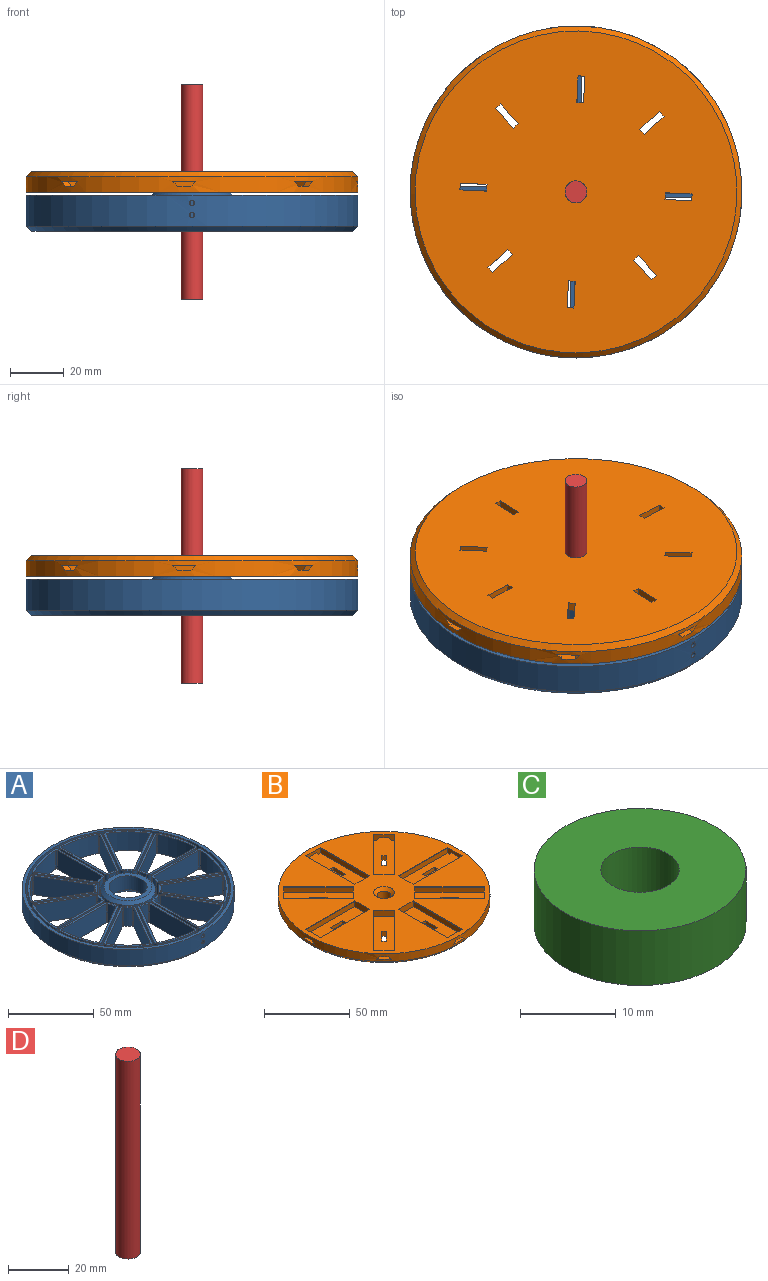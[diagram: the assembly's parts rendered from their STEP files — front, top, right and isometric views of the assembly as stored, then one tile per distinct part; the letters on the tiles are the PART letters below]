
ASSEMBLY  parts=4 mates=4
PART A: 223 faces, bbox 123.9x123.9x14.7 mm
  f0: plane 119.88x119.88mm, normal (0,0,1), area 1334.9mm2, adj f4,f6,f7,f8,f9,f10,f11,f12
  f1: cylinder r=11.1mm len=22.2mm, axis (0,0,-1), area 700mm2, adj f211,f213
  f2: cylinder r=61.94mm len=123.88mm, axis (0,0,-1), area 4468.3mm2, adj f5,f212,f215,f216,f217,f218,f219,f220
  f3: plane 120.15x120.15mm, normal (0,0,-1), area 3116.5mm2, adj f114,f115,f116,f117,f118,f119,f120,f121
  f4: cylinder r=59.94mm len=119.88mm, axis (0,0,-1), area 3758.9mm2, adj f0,f5,f215,f216,f217,f218,f219,f220
  f5: plane 123.88x123.88mm, normal (0,0,1), area 765.8mm2, adj f2,f4
  f6: plane 36.7x10mm, normal (0,1,0), area 367mm2, adj f0,f7,f13,f14
  f7: cylinder r=2mm len=10mm, axis (0,0,-1), area 28.8mm2, adj f0,f6,f8,f14
  f8: cylinder r=18.01mm len=10mm, axis (0,0,-1), area 47.4mm2, adj f0,f7,f9,f14
  f9: cylinder r=2mm len=10mm, axis (0,0,-1), area 28.8mm2, adj f0,f8,f10,f14
  f10: plane 31.79x18.35mm, normal (-0.5,-0.87,0), area 367mm2, adj f0,f9,f11,f14
  f11: cylinder r=2mm len=10mm, axis (0,0,-1), area 32.3mm2, adj f0,f10,f12,f14
  f12: cylinder r=58.6mm len=24.25mm, axis (0,0,-1), area 253mm2, adj f0,f11,f13,f14
  f13: cylinder r=2mm len=10mm, axis (0,0,-1), area 32.3mm2, adj f0,f6,f12,f14
  f14: plane 42.06x27.42mm, normal (0,0,1), area 145.1mm2, adj f6,f7,f8,f9,f10,f11,f12,f13
  f15: plane 31.79x18.35mm, normal (-0.5,0.87,0), area 367mm2, adj f0,f16,f22,f23
  f16: cylinder r=2mm len=10mm, axis (0,0,-1), area 28.8mm2, adj f0,f15,f17,f23
  f17: cylinder r=18.01mm len=10mm, axis (0,0,-1), area 47.4mm2, adj f0,f16,f18,f23
  f18: cylinder r=2mm len=10mm, axis (0,0,-1), area 28.8mm2, adj f0,f17,f19,f23
  f19: plane 36.7x10mm, normal (0,-1,0), area 367mm2, adj f0,f18,f20,f23
  f20: cylinder r=2mm len=10mm, axis (0,0,-1), area 32.3mm2, adj f0,f19,f21,f23
  f21: cylinder r=58.6mm len=24.25mm, axis (0,0,-1), area 253mm2, adj f0,f20,f22,f23
  f22: cylinder r=2mm len=10mm, axis (0,0,-1), area 32.3mm2, adj f0,f15,f21,f23
  f23: plane 42.06x27.42mm, normal (0,0,1), area 145.1mm2, adj f15,f16,f17,f18,f19,f20,f21,f22
  f24: plane 31.79x18.35mm, normal (-0.87,0.5,0), area 367mm2, adj f0,f25,f31,f32
  f25: cylinder r=2mm len=10mm, axis (0,0,-1), area 28.8mm2, adj f0,f24,f26,f32
  f26: cylinder r=18.01mm len=10mm, axis (0,0,-1), area 47.4mm2, adj f0,f25,f27,f32
  f27: cylinder r=2mm len=10mm, axis (0,0,-1), area 28.8mm2, adj f0,f26,f28,f32
  f28: plane 31.79x18.35mm, normal (0.5,-0.87,0), area 367mm2, adj f0,f27,f29,f32
  f29: cylinder r=2mm len=10mm, axis (0,0,-1), area 32.3mm2, adj f0,f28,f30,f32
  f30: cylinder r=58.6mm len=17.75mm, axis (0,0,-1), area 253mm2, adj f0,f29,f31,f32
  f31: cylinder r=2mm len=10mm, axis (0,0,-1), area 32.3mm2, adj f0,f24,f30,f32
  f32: plane 39.5x39.5mm, normal (0,0,1), area 145.1mm2, adj f24,f25,f26,f27,f28,f29,f30,f31
  f33: plane 36.7x10mm, normal (-1,0,0), area 367mm2, adj f0,f34,f40,f41
  f34: cylinder r=2mm len=10mm, axis (0,0,-1), area 28.8mm2, adj f0,f33,f35,f41
  f35: cylinder r=18.01mm len=10mm, axis (0,0,-1), area 47.4mm2, adj f0,f34,f36,f41
  f36: cylinder r=2mm len=10mm, axis (0,0,-1), area 28.8mm2, adj f0,f35,f37,f41
  f37: plane 31.79x18.35mm, normal (0.87,-0.5,0), area 367mm2, adj f0,f36,f38,f41
  f38: cylinder r=2mm len=10mm, axis (0,0,-1), area 32.3mm2, adj f0,f37,f39,f41
  f39: cylinder r=58.6mm len=24.25mm, axis (0,0,-1), area 253mm2, adj f0,f38,f40,f41
  f40: cylinder r=2mm len=10mm, axis (0,0,-1), area 32.3mm2, adj f0,f33,f39,f41
  f41: plane 42.06x27.42mm, normal (0,0,1), area 145.1mm2, adj f33,f34,f35,f36,f37,f38,f39,f40
  f42: plane 31.79x18.35mm, normal (-0.87,-0.5,0), area 367mm2, adj f0,f43,f49,f50
  f43: cylinder r=2mm len=10mm, axis (0,0,-1), area 28.8mm2, adj f0,f42,f44,f50
  f44: cylinder r=18.01mm len=10mm, axis (0,0,-1), area 47.4mm2, adj f0,f43,f45,f50
  f45: cylinder r=2mm len=10mm, axis (0,0,-1), area 28.8mm2, adj f0,f44,f46,f50
  f46: plane 36.7x10mm, normal (1,0,0), area 367mm2, adj f0,f45,f47,f50
  f47: cylinder r=2mm len=10mm, axis (0,0,-1), area 32.3mm2, adj f0,f46,f48,f50
  f48: cylinder r=58.6mm len=24.25mm, axis (0,0,-1), area 253mm2, adj f0,f47,f49,f50
  f49: cylinder r=2mm len=10mm, axis (0,0,-1), area 32.3mm2, adj f0,f42,f48,f50
  f50: plane 42.06x27.42mm, normal (0,0,1), area 145.1mm2, adj f42,f43,f44,f45,f46,f47,f48,f49
  f51: plane 31.79x18.35mm, normal (-0.5,-0.87,0), area 367mm2, adj f0,f52,f58,f59
  f52: cylinder r=2mm len=10mm, axis (0,0,-1), area 28.8mm2, adj f0,f51,f53,f59
  f53: cylinder r=18.01mm len=10mm, axis (0,0,-1), area 47.4mm2, adj f0,f52,f54,f59
  f54: cylinder r=2mm len=10mm, axis (0,0,-1), area 28.8mm2, adj f0,f53,f55,f59
  f55: plane 31.79x18.35mm, normal (0.87,0.5,0), area 367mm2, adj f0,f54,f56,f59
  f56: cylinder r=2mm len=10mm, axis (0,0,-1), area 32.3mm2, adj f0,f55,f57,f59
  f57: cylinder r=58.6mm len=17.75mm, axis (0,0,-1), area 253mm2, adj f0,f56,f58,f59
  f58: cylinder r=2mm len=10mm, axis (0,0,-1), area 32.3mm2, adj f0,f51,f57,f59
  f59: plane 39.5x39.5mm, normal (0,0,1), area 145.1mm2, adj f51,f52,f53,f54,f55,f56,f57,f58
  f60: plane 36.7x10mm, normal (0,-1,0), area 367mm2, adj f0,f61,f67,f68
  f61: cylinder r=2mm len=10mm, axis (0,0,-1), area 28.8mm2, adj f0,f60,f62,f68
  f62: cylinder r=18.01mm len=10mm, axis (0,0,-1), area 47.4mm2, adj f0,f61,f63,f68
  f63: cylinder r=2mm len=10mm, axis (0,0,-1), area 28.8mm2, adj f0,f62,f64,f68
  f64: plane 31.79x18.35mm, normal (0.5,0.87,0), area 367mm2, adj f0,f63,f65,f68
  f65: cylinder r=2mm len=10mm, axis (0,0,-1), area 32.3mm2, adj f0,f64,f66,f68
  f66: cylinder r=58.6mm len=24.25mm, axis (0,0,-1), area 253mm2, adj f0,f65,f67,f68
  f67: cylinder r=2mm len=10mm, axis (0,0,-1), area 32.3mm2, adj f0,f60,f66,f68
  f68: plane 42.06x27.42mm, normal (0,0,1), area 145.1mm2, adj f60,f61,f62,f63,f64,f65,f66,f67
  f69: plane 31.79x18.35mm, normal (0.5,-0.87,0), area 367mm2, adj f0,f70,f76,f77
  f70: cylinder r=2mm len=10mm, axis (0,0,-1), area 28.8mm2, adj f0,f69,f71,f77
  f71: cylinder r=18.01mm len=10mm, axis (0,0,-1), area 47.4mm2, adj f0,f70,f72,f77
  f72: cylinder r=2mm len=10mm, axis (0,0,-1), area 28.8mm2, adj f0,f71,f73,f77
  f73: plane 36.7x10mm, normal (0,1,0), area 367mm2, adj f0,f72,f74,f77
  f74: cylinder r=2mm len=10mm, axis (0,0,-1), area 32.3mm2, adj f0,f73,f75,f77
  f75: cylinder r=58.6mm len=24.25mm, axis (0,0,-1), area 253mm2, adj f0,f74,f76,f77
  f76: cylinder r=2mm len=10mm, axis (0,0,-1), area 32.3mm2, adj f0,f69,f75,f77
  f77: plane 42.06x27.42mm, normal (0,0,1), area 145.1mm2, adj f69,f70,f71,f72,f73,f74,f75,f76
  f78: plane 31.79x18.35mm, normal (0.87,-0.5,0), area 367mm2, adj f0,f79,f85,f86
  f79: cylinder r=2mm len=10mm, axis (0,0,-1), area 28.8mm2, adj f0,f78,f80,f86
  f80: cylinder r=18.01mm len=10mm, axis (0,0,-1), area 47.4mm2, adj f0,f79,f81,f86
  f81: cylinder r=2mm len=10mm, axis (0,0,-1), area 28.8mm2, adj f0,f80,f82,f86
  f82: plane 31.79x18.35mm, normal (-0.5,0.87,0), area 367mm2, adj f0,f81,f83,f86
  f83: cylinder r=2mm len=10mm, axis (0,0,-1), area 32.3mm2, adj f0,f82,f84,f86
  f84: cylinder r=58.6mm len=17.75mm, axis (0,0,-1), area 253mm2, adj f0,f83,f85,f86
  f85: cylinder r=2mm len=10mm, axis (0,0,-1), area 32.3mm2, adj f0,f78,f84,f86
  f86: plane 39.5x39.5mm, normal (0,0,1), area 145.1mm2, adj f78,f79,f80,f81,f82,f83,f84,f85
  f87: plane 36.7x10mm, normal (1,0,0), area 367mm2, adj f0,f88,f94,f95
  f88: cylinder r=2mm len=10mm, axis (0,0,-1), area 28.8mm2, adj f0,f87,f89,f95
  f89: cylinder r=18.01mm len=10mm, axis (0,0,-1), area 47.4mm2, adj f0,f88,f90,f95
  f90: cylinder r=2mm len=10mm, axis (0,0,-1), area 28.8mm2, adj f0,f89,f91,f95
  f91: plane 31.79x18.35mm, normal (-0.87,0.5,0), area 367mm2, adj f0,f90,f92,f95
  f92: cylinder r=2mm len=10mm, axis (0,0,-1), area 32.3mm2, adj f0,f91,f93,f95
  f93: cylinder r=58.6mm len=24.25mm, axis (0,0,-1), area 253mm2, adj f0,f92,f94,f95
  f94: cylinder r=2mm len=10mm, axis (0,0,-1), area 32.3mm2, adj f0,f87,f93,f95
  f95: plane 42.06x27.42mm, normal (0,0,1), area 145.1mm2, adj f87,f88,f89,f90,f91,f92,f93,f94
  f96: plane 31.79x18.35mm, normal (0.87,0.5,0), area 367mm2, adj f0,f97,f103,f104
  f97: cylinder r=2mm len=10mm, axis (0,0,-1), area 28.8mm2, adj f0,f96,f98,f104
  f98: cylinder r=18.01mm len=10mm, axis (0,0,-1), area 47.4mm2, adj f0,f97,f99,f104
  f99: cylinder r=2mm len=10mm, axis (0,0,-1), area 28.8mm2, adj f0,f98,f100,f104
  f100: plane 36.7x10mm, normal (-1,0,0), area 367mm2, adj f0,f99,f101,f104
  f101: cylinder r=2mm len=10mm, axis (0,0,-1), area 32.3mm2, adj f0,f100,f102,f104
  f102: cylinder r=58.6mm len=24.25mm, axis (0,0,-1), area 253mm2, adj f0,f101,f103,f104
  f103: cylinder r=2mm len=10mm, axis (0,0,-1), area 32.3mm2, adj f0,f96,f102,f104
  f104: plane 42.06x27.42mm, normal (0,0,1), area 145.1mm2, adj f96,f97,f98,f99,f100,f101,f102,f103
  f105: plane 31.79x18.35mm, normal (0.5,0.87,0), area 367mm2, adj f0,f106,f112,f113
  f106: cylinder r=2mm len=10mm, axis (0,0,-1), area 28.8mm2, adj f0,f105,f107,f113
  f107: cylinder r=18.01mm len=10mm, axis (0,0,-1), area 47.4mm2, adj f0,f106,f108,f113
  f108: cylinder r=2mm len=10mm, axis (0,0,-1), area 28.8mm2, adj f0,f107,f109,f113
  f109: plane 31.79x18.35mm, normal (-0.87,-0.5,0), area 367mm2, adj f0,f108,f110,f113
  f110: cylinder r=2mm len=10mm, axis (0,0,-1), area 32.3mm2, adj f0,f109,f111,f113
  f111: cylinder r=58.6mm len=17.75mm, axis (0,0,-1), area 253mm2, adj f0,f110,f112,f113
  f112: cylinder r=2mm len=10mm, axis (0,0,-1), area 32.3mm2, adj f0,f105,f111,f113
  f113: plane 39.5x39.5mm, normal (0,0,1), area 145.1mm2, adj f105,f106,f107,f108,f109,f110,f111,f112
  f114: cylinder r=19.31mm len=13.5mm, axis (0,0,1), area 68.6mm2, adj f3,f113,f115,f121
  f115: cylinder r=0.7mm len=13.5mm, axis (0,0,1), area 13.6mm2, adj f3,f113,f114,f116
  f116: plane 31.79x18.35mm, normal (0.87,0.5,0), area 495.5mm2, adj f3,f113,f115,f117
  f117: cylinder r=0.7mm len=13.5mm, axis (0,0,1), area 15.3mm2, adj f3,f113,f116,f118
  f118: cylinder r=57.3mm len=17.36mm, axis (0,0,1), area 334mm2, adj f3,f113,f117,f119
  f119: cylinder r=0.7mm len=13.5mm, axis (0,0,1), area 15.3mm2, adj f3,f113,f118,f120
  f120: plane 31.79x18.35mm, normal (-0.5,-0.87,0), area 495.5mm2, adj f3,f113,f119,f121
  f121: cylinder r=0.7mm len=13.5mm, axis (0,0,1), area 13.6mm2, adj f3,f113,f114,f120
  f122: cylinder r=19.31mm len=13.5mm, axis (0,0,1), area 68.6mm2, adj f3,f104,f123,f129
  f123: cylinder r=0.7mm len=13.5mm, axis (0,0,1), area 13.6mm2, adj f3,f104,f122,f124
  f124: plane 36.7x13.5mm, normal (1,0,0), area 495.5mm2, adj f3,f104,f123,f125
  f125: cylinder r=0.7mm len=13.5mm, axis (0,0,1), area 15.3mm2, adj f3,f104,f124,f126
  f126: cylinder r=57.3mm len=23.71mm, axis (0,0,1), area 334mm2, adj f3,f104,f125,f127
  f127: cylinder r=0.7mm len=13.5mm, axis (0,0,1), area 15.3mm2, adj f3,f104,f126,f128
  f128: plane 31.79x18.35mm, normal (-0.87,-0.5,0), area 495.5mm2, adj f3,f104,f127,f129
  f129: cylinder r=0.7mm len=13.5mm, axis (0,0,1), area 13.6mm2, adj f3,f104,f122,f128
  f130: cylinder r=19.31mm len=13.5mm, axis (0,0,1), area 68.6mm2, adj f3,f95,f131,f137
  f131: cylinder r=0.7mm len=13.5mm, axis (0,0,1), area 13.6mm2, adj f3,f95,f130,f132
  f132: plane 31.79x18.35mm, normal (0.87,-0.5,0), area 495.5mm2, adj f3,f95,f131,f133
  f133: cylinder r=0.7mm len=13.5mm, axis (0,0,1), area 15.3mm2, adj f3,f95,f132,f134
  f134: cylinder r=57.3mm len=23.71mm, axis (0,0,1), area 334mm2, adj f3,f95,f133,f135
  f135: cylinder r=0.7mm len=13.5mm, axis (0,0,1), area 15.3mm2, adj f3,f95,f134,f136
  f136: plane 36.7x13.5mm, normal (-1,0,0), area 495.5mm2, adj f3,f95,f135,f137
  f137: cylinder r=0.7mm len=13.5mm, axis (0,0,1), area 13.6mm2, adj f3,f95,f130,f136
  f138: cylinder r=19.31mm len=13.5mm, axis (0,0,1), area 68.6mm2, adj f3,f86,f139,f145
  f139: cylinder r=0.7mm len=13.5mm, axis (0,0,1), area 13.6mm2, adj f3,f86,f138,f140
  f140: plane 31.79x18.35mm, normal (0.5,-0.87,0), area 495.5mm2, adj f3,f86,f139,f141
  f141: cylinder r=0.7mm len=13.5mm, axis (0,0,1), area 15.3mm2, adj f3,f86,f140,f142
  f142: cylinder r=57.3mm len=17.36mm, axis (0,0,1), area 334mm2, adj f3,f86,f141,f143
  f143: cylinder r=0.7mm len=13.5mm, axis (0,0,1), area 15.3mm2, adj f3,f86,f142,f144
  f144: plane 31.79x18.35mm, normal (-0.87,0.5,0), area 495.5mm2, adj f3,f86,f143,f145
  f145: cylinder r=0.7mm len=13.5mm, axis (0,0,1), area 13.6mm2, adj f3,f86,f138,f144
  f146: cylinder r=19.31mm len=13.5mm, axis (0,0,1), area 68.6mm2, adj f3,f77,f147,f153
  f147: cylinder r=0.7mm len=13.5mm, axis (0,0,1), area 13.6mm2, adj f3,f77,f146,f148
  f148: plane 36.7x13.5mm, normal (0,-1,0), area 495.5mm2, adj f3,f77,f147,f149
  f149: cylinder r=0.7mm len=13.5mm, axis (0,0,1), area 15.3mm2, adj f3,f77,f148,f150
  f150: cylinder r=57.3mm len=23.71mm, axis (0,0,1), area 334mm2, adj f3,f77,f149,f151
  f151: cylinder r=0.7mm len=13.5mm, axis (0,0,1), area 15.3mm2, adj f3,f77,f150,f152
  f152: plane 31.79x18.35mm, normal (-0.5,0.87,0), area 495.5mm2, adj f3,f77,f151,f153
  f153: cylinder r=0.7mm len=13.5mm, axis (0,0,1), area 13.6mm2, adj f3,f77,f146,f152
  f154: cylinder r=19.31mm len=13.5mm, axis (0,0,1), area 68.6mm2, adj f3,f68,f155,f161
  f155: cylinder r=0.7mm len=13.5mm, axis (0,0,1), area 13.6mm2, adj f3,f68,f154,f156
  f156: plane 31.79x18.35mm, normal (-0.5,-0.87,0), area 495.5mm2, adj f3,f68,f155,f157
  f157: cylinder r=0.7mm len=13.5mm, axis (0,0,1), area 15.3mm2, adj f3,f68,f156,f158
  f158: cylinder r=57.3mm len=23.71mm, axis (0,0,1), area 334mm2, adj f3,f68,f157,f159
  f159: cylinder r=0.7mm len=13.5mm, axis (0,0,1), area 15.3mm2, adj f3,f68,f158,f160
  f160: plane 36.7x13.5mm, normal (0,1,0), area 495.5mm2, adj f3,f68,f159,f161
  f161: cylinder r=0.7mm len=13.5mm, axis (0,0,1), area 13.6mm2, adj f3,f68,f154,f160
  f162: cylinder r=19.31mm len=13.5mm, axis (0,0,1), area 68.6mm2, adj f3,f59,f163,f169
  f163: cylinder r=0.7mm len=13.5mm, axis (0,0,1), area 13.6mm2, adj f3,f59,f162,f164
  f164: plane 31.79x18.35mm, normal (-0.87,-0.5,0), area 495.5mm2, adj f3,f59,f163,f165
  f165: cylinder r=0.7mm len=13.5mm, axis (0,0,1), area 15.3mm2, adj f3,f59,f164,f166
  f166: cylinder r=57.3mm len=17.36mm, axis (0,0,1), area 334mm2, adj f3,f59,f165,f167
  f167: cylinder r=0.7mm len=13.5mm, axis (0,0,1), area 15.3mm2, adj f3,f59,f166,f168
  f168: plane 31.79x18.35mm, normal (0.5,0.87,0), area 495.5mm2, adj f3,f59,f167,f169
  f169: cylinder r=0.7mm len=13.5mm, axis (0,0,1), area 13.6mm2, adj f3,f59,f162,f168
  f170: cylinder r=19.31mm len=13.5mm, axis (0,0,1), area 68.6mm2, adj f3,f50,f171,f177
  f171: cylinder r=0.7mm len=13.5mm, axis (0,0,1), area 13.6mm2, adj f3,f50,f170,f172
  f172: plane 36.7x13.5mm, normal (-1,0,0), area 495.5mm2, adj f3,f50,f171,f173
  f173: cylinder r=0.7mm len=13.5mm, axis (0,0,1), area 15.3mm2, adj f3,f50,f172,f174
  f174: cylinder r=57.3mm len=23.71mm, axis (0,0,1), area 334mm2, adj f3,f50,f173,f175
  f175: cylinder r=0.7mm len=13.5mm, axis (0,0,1), area 15.3mm2, adj f3,f50,f174,f176
  f176: plane 31.79x18.35mm, normal (0.87,0.5,0), area 495.5mm2, adj f3,f50,f175,f177
  f177: cylinder r=0.7mm len=13.5mm, axis (0,0,1), area 13.6mm2, adj f3,f50,f170,f176
  f178: cylinder r=19.31mm len=13.5mm, axis (0,0,1), area 68.6mm2, adj f3,f41,f179,f185
  f179: cylinder r=0.7mm len=13.5mm, axis (0,0,1), area 13.6mm2, adj f3,f41,f178,f180
  f180: plane 31.79x18.35mm, normal (-0.87,0.5,0), area 495.5mm2, adj f3,f41,f179,f181
  f181: cylinder r=0.7mm len=13.5mm, axis (0,0,1), area 15.3mm2, adj f3,f41,f180,f182
  f182: cylinder r=57.3mm len=23.71mm, axis (0,0,1), area 334mm2, adj f3,f41,f181,f183
  f183: cylinder r=0.7mm len=13.5mm, axis (0,0,1), area 15.3mm2, adj f3,f41,f182,f184
  f184: plane 36.7x13.5mm, normal (1,0,0), area 495.5mm2, adj f3,f41,f183,f185
  f185: cylinder r=0.7mm len=13.5mm, axis (0,0,1), area 13.6mm2, adj f3,f41,f178,f184
  f186: cylinder r=19.31mm len=13.5mm, axis (0,0,1), area 68.6mm2, adj f3,f32,f187,f193
  f187: cylinder r=0.7mm len=13.5mm, axis (0,0,1), area 13.6mm2, adj f3,f32,f186,f188
  f188: plane 31.79x18.35mm, normal (-0.5,0.87,0), area 495.5mm2, adj f3,f32,f187,f189
  f189: cylinder r=0.7mm len=13.5mm, axis (0,0,1), area 15.3mm2, adj f3,f32,f188,f190
  f190: cylinder r=57.3mm len=17.36mm, axis (0,0,1), area 334mm2, adj f3,f32,f189,f191
  f191: cylinder r=0.7mm len=13.5mm, axis (0,0,1), area 15.3mm2, adj f3,f32,f190,f192
  f192: plane 31.79x18.35mm, normal (0.87,-0.5,0), area 495.5mm2, adj f3,f32,f191,f193
  f193: cylinder r=0.7mm len=13.5mm, axis (0,0,1), area 13.6mm2, adj f3,f32,f186,f192
  f194: cylinder r=19.31mm len=13.5mm, axis (0,0,1), area 68.6mm2, adj f3,f23,f195,f201
  f195: cylinder r=0.7mm len=13.5mm, axis (0,0,1), area 13.6mm2, adj f3,f23,f194,f196
  f196: plane 36.7x13.5mm, normal (0,1,0), area 495.5mm2, adj f3,f23,f195,f197
  f197: cylinder r=0.7mm len=13.5mm, axis (0,0,1), area 15.3mm2, adj f3,f23,f196,f198
  f198: cylinder r=57.3mm len=23.71mm, axis (0,0,1), area 334mm2, adj f3,f23,f197,f199
  f199: cylinder r=0.7mm len=13.5mm, axis (0,0,1), area 15.3mm2, adj f3,f23,f198,f200
  f200: plane 31.79x18.35mm, normal (0.5,-0.87,0), area 495.5mm2, adj f3,f23,f199,f201
  f201: cylinder r=0.7mm len=13.5mm, axis (0,0,1), area 13.6mm2, adj f3,f23,f194,f200
  f202: plane 36.7x13.5mm, normal (0,-1,0), area 495.5mm2, adj f3,f14,f203,f209
  f203: cylinder r=0.7mm len=13.5mm, axis (0,0,1), area 13.6mm2, adj f3,f14,f202,f204
  f204: cylinder r=19.31mm len=13.5mm, axis (0,0,1), area 68.6mm2, adj f3,f14,f203,f205
  f205: cylinder r=0.7mm len=13.5mm, axis (0,0,1), area 13.6mm2, adj f3,f14,f204,f206
  f206: plane 31.79x18.35mm, normal (0.5,0.87,0), area 495.5mm2, adj f3,f14,f205,f207
  f207: cylinder r=0.7mm len=13.5mm, axis (0,0,1), area 15.3mm2, adj f3,f14,f206,f208
  f208: cylinder r=57.3mm len=23.71mm, axis (0,0,1), area 334mm2, adj f3,f14,f207,f209
  f209: cylinder r=0.7mm len=13.5mm, axis (0,0,1), area 15.3mm2, adj f3,f14,f202,f208
  f210: cylinder r=16mm len=32mm, axis (0,0,-1), area 924.9mm2, adj f0,f214
  f211: plane 28x28mm, normal (0,0,1), area 228.7mm2, adj f1,f214
  f212: cone r=61.94mm half-angle=43deg, axis (0,0,1), area 1048.2mm2, adj f2,f3
  f213: cone r=16.1mm half-angle=47deg, axis (0,0,-1), area 584.2mm2, adj f1,f3
  f214: cone r=14mm half-angle=45deg, axis (0,0,-1), area 266.6mm2, adj f210,f211
  f215: plane 2x0.49mm, normal (1,0,0), area 1mm2, adj f2,f4,f216,f218
  f216: cylinder r=1mm len=2mm, axis (0,-1,0), area 9.4mm2, adj f2,f4,f215,f217
  f217: plane 2x0.49mm, normal (-1,0,0), area 1mm2, adj f2,f4,f216,f218
  f218: plane 2x1.41mm, normal (0,0,-1), area 2.8mm2, adj f2,f4,f215,f217
  f219: plane 2x0.49mm, normal (1,0,0), area 1mm2, adj f2,f4,f220,f222
  f220: cylinder r=1mm len=2mm, axis (0,-1,0), area 9.4mm2, adj f2,f4,f219,f221
  f221: plane 2x0.49mm, normal (-1,0,0), area 1mm2, adj f2,f4,f220,f222
  f222: plane 2x1.41mm, normal (0,0,-1), area 2.8mm2, adj f2,f4,f219,f221
PART B: 134 faces, bbox 123.9x123.9x7.6 mm
  f0: plane 8.91x8.91mm, normal (-0.71,0.71,0), area 37.7mm2, adj f1,f2,f30,f75,f101,f102,f103,f128
  f1: plane 28.71x28.71mm, normal (-0.71,-0.71,0), area 146.2mm2, adj f0,f30,f72,f130
  f2: plane 28.71x28.71mm, normal (0.71,0.71,0), area 146.2mm2, adj f0,f30,f72,f129
  f3: plane 12.6x4.1mm, normal (-1,0,0), area 37.7mm2, adj f4,f5,f31,f75,f98,f99,f100,f124
  f4: plane 40.6x3.6mm, normal (0,-1,0), area 146.2mm2, adj f3,f31,f73,f126
  f5: plane 40.6x3.6mm, normal (0,1,0), area 146.2mm2, adj f3,f31,f73,f125
  f6: plane 8.91x8.91mm, normal (-0.71,-0.71,0), area 37.7mm2, adj f7,f8,f32,f75,f95,f96,f97,f120
  f7: plane 28.71x28.71mm, normal (0.71,-0.71,0), area 146.2mm2, adj f6,f32,f74,f122
  f8: plane 28.71x28.71mm, normal (-0.71,0.71,0), area 146.2mm2, adj f6,f32,f74,f121
  f9: plane 12.6x4.1mm, normal (0,-1,0), area 37.7mm2, adj f10,f11,f25,f75,f92,f93,f94,f116
  f10: plane 40.6x3.6mm, normal (1,0,0), area 146.2mm2, adj f9,f25,f67,f118
  f11: plane 40.6x3.6mm, normal (-1,0,0), area 146.2mm2, adj f9,f25,f67,f117
  f12: plane 8.91x8.91mm, normal (0.71,-0.71,0), area 37.7mm2, adj f13,f14,f26,f75,f89,f90,f91,f112
  f13: plane 28.71x28.71mm, normal (0.71,0.71,0), area 146.2mm2, adj f12,f26,f68,f114
  f14: plane 28.71x28.71mm, normal (-0.71,-0.71,0), area 146.2mm2, adj f12,f26,f68,f113
  f15: plane 12.6x4.1mm, normal (1,0,0), area 37.7mm2, adj f16,f17,f27,f75,f86,f87,f88,f108
  f16: plane 40.6x3.6mm, normal (0,1,0), area 146.2mm2, adj f15,f27,f69,f110
  f17: plane 40.6x3.6mm, normal (0,-1,0), area 146.2mm2, adj f15,f27,f69,f109
  f18: plane 8.91x8.91mm, normal (0.71,0.71,0), area 37.7mm2, adj f19,f20,f28,f75,f83,f84,f85,f104
  f19: plane 28.71x28.71mm, normal (-0.71,0.71,0), area 146.2mm2, adj f18,f28,f70,f106
  f20: plane 28.71x28.71mm, normal (0.71,-0.71,0), area 146.2mm2, adj f18,f28,f70,f105
  f21: cylinder r=61.94mm len=123.88mm, axis (0,0,-1), area 2069.4mm2, adj f25,f26,f27,f28,f29,f30,f31,f32
  f22: plane 12.6x4.1mm, normal (0,1,0), area 37.7mm2, adj f23,f24,f29,f75,f76,f77,f78,f79
  f23: plane 40.6x3.6mm, normal (-1,0,0), area 146.2mm2, adj f22,f29,f71,f78
  f24: plane 40.6x3.6mm, normal (1,0,0), area 146.2mm2, adj f22,f29,f71,f77
  f25: plane 43.94x12.6mm, normal (0,0,1), area 515.3mm2, adj f9,f10,f11,f21,f48,f49,f50,f63
  f26: plane 38.5x38.5mm, normal (0,0,1), area 515.3mm2, adj f12,f13,f14,f21,f45,f46,f47,f62
  f27: plane 43.94x12.6mm, normal (0,0,1), area 515.3mm2, adj f15,f16,f17,f21,f42,f43,f44,f61
  f28: plane 38.5x38.5mm, normal (0,0,1), area 515.3mm2, adj f18,f19,f20,f21,f39,f40,f41,f60
  f29: plane 43.94x12.6mm, normal (0,0,1), area 515.3mm2, adj f21,f22,f23,f24,f36,f37,f38,f59
  f30: plane 38.5x38.5mm, normal (0,0,1), area 515.3mm2, adj f0,f1,f2,f21,f33,f34,f35,f58
  f31: plane 43.94x12.6mm, normal (0,0,1), area 515.3mm2, adj f3,f4,f5,f21,f54,f55,f56,f65
  f32: plane 38.5x38.5mm, normal (0,0,1), area 515.3mm2, adj f6,f7,f8,f21,f51,f52,f53,f64
  f33: plane 7.07x7.07mm, normal (0.71,0.71,0), area 35mm2, adj f30,f34,f58,f66
  f34: plane 3.5x1.77mm, normal (0.71,-0.71,0), area 8.8mm2, adj f30,f33,f35,f66
  f35: plane 7.07x7.07mm, normal (-0.71,-0.71,0), area 35mm2, adj f30,f34,f58,f66
  f36: plane 10x3.5mm, normal (1,0,0), area 35mm2, adj f29,f37,f59,f66
  f37: plane 3.5x2.5mm, normal (0,-1,0), area 8.8mm2, adj f29,f36,f38,f66
  f38: plane 10x3.5mm, normal (-1,0,0), area 35mm2, adj f29,f37,f59,f66
  f39: plane 7.07x7.07mm, normal (0.71,-0.71,0), area 35mm2, adj f28,f40,f60,f66
  f40: plane 3.5x1.77mm, normal (-0.71,-0.71,0), area 8.8mm2, adj f28,f39,f41,f66
  f41: plane 7.07x7.07mm, normal (-0.71,0.71,0), area 35mm2, adj f28,f40,f60,f66
  f42: plane 10x3.5mm, normal (0,-1,0), area 35mm2, adj f27,f43,f61,f66
  f43: plane 3.5x2.5mm, normal (-1,0,0), area 8.8mm2, adj f27,f42,f44,f66
  f44: plane 10x3.5mm, normal (0,1,0), area 35mm2, adj f27,f43,f61,f66
  f45: plane 7.07x7.07mm, normal (-0.71,-0.71,0), area 35mm2, adj f26,f46,f62,f66
  f46: plane 3.5x1.77mm, normal (-0.71,0.71,0), area 8.8mm2, adj f26,f45,f47,f66
  f47: plane 7.07x7.07mm, normal (0.71,0.71,0), area 35mm2, adj f26,f46,f62,f66
  f48: plane 10x3.5mm, normal (-1,0,0), area 35mm2, adj f25,f49,f63,f66
  f49: plane 3.5x2.5mm, normal (0,1,0), area 8.8mm2, adj f25,f48,f50,f66
  f50: plane 10x3.5mm, normal (1,0,0), area 35mm2, adj f25,f49,f63,f66
  f51: plane 7.07x7.07mm, normal (-0.71,0.71,0), area 35mm2, adj f32,f52,f64,f66
  f52: plane 3.5x1.77mm, normal (0.71,0.71,0), area 8.8mm2, adj f32,f51,f53,f66
  f53: plane 7.07x7.07mm, normal (0.71,-0.71,0), area 35mm2, adj f32,f52,f64,f66
  f54: plane 3.5x2.5mm, normal (1,0,0), area 8.8mm2, adj f31,f55,f65,f66
  f55: plane 10x3.5mm, normal (0,-1,0), area 35mm2, adj f31,f54,f56,f66
  f56: plane 3.5x2.5mm, normal (-1,0,0), area 8.8mm2, adj f31,f55,f65,f66
  f57: cylinder r=4.1mm len=8.2mm, axis (0,0,-1), area 144.3mm2, adj f66,f133
  f58: plane 3.5x1.77mm, normal (-0.71,0.71,0), area 8.8mm2, adj f30,f33,f35,f66
  f59: plane 3.5x2.5mm, normal (0,1,0), area 8.8mm2, adj f29,f36,f38,f66
  f60: plane 3.5x1.77mm, normal (0.71,0.71,0), area 8.8mm2, adj f28,f39,f41,f66
  f61: plane 3.5x2.5mm, normal (1,0,0), area 8.8mm2, adj f27,f42,f44,f66
  f62: plane 3.5x1.77mm, normal (0.71,-0.71,0), area 8.8mm2, adj f26,f45,f47,f66
  f63: plane 3.5x2.5mm, normal (0,-1,0), area 8.8mm2, adj f25,f48,f50,f66
  f64: plane 3.5x1.77mm, normal (-0.71,-0.71,0), area 8.8mm2, adj f32,f51,f53,f66
  f65: plane 10x3.5mm, normal (0,1,0), area 35mm2, adj f31,f54,f56,f66
  f66: plane 120.15x120.15mm, normal (0,0,-1), area 11084.3mm2, adj f33,f34,f35,f36,f37,f38,f39,f40
  f67: plane 12.6x4.1mm, normal (0,1,0), area 51.5mm2, adj f10,f11,f25,f75,f116,f117,f118,f119
  f68: plane 8.91x8.91mm, normal (-0.71,0.71,0), area 51.5mm2, adj f13,f14,f26,f75,f112,f113,f114,f115
  f69: plane 12.6x4.1mm, normal (-1,0,0), area 51.5mm2, adj f16,f17,f27,f75,f108,f109,f110,f111
  f70: plane 8.91x8.91mm, normal (-0.71,-0.71,0), area 51.5mm2, adj f19,f20,f28,f75,f104,f105,f106,f107
  f71: plane 12.6x4.1mm, normal (0,-1,0), area 51.5mm2, adj f23,f24,f29,f75,f76,f77,f78,f79
  f72: plane 8.91x8.91mm, normal (0.71,-0.71,0), area 51.5mm2, adj f1,f2,f30,f75,f128,f129,f130,f131
  f73: plane 12.6x4.1mm, normal (1,0,0), area 51.5mm2, adj f4,f5,f31,f75,f124,f125,f126,f127
  f74: plane 8.91x8.91mm, normal (0.71,0.71,0), area 51.5mm2, adj f7,f8,f32,f75,f120,f121,f122,f123
  f75: plane 123.88x123.88mm, normal (0,0,1), area 8037.5mm2, adj f0,f3,f6,f9,f12,f15,f18,f21
  f76: plane 40.6x0.19mm, normal (1,0,0), area 7.7mm2, adj f22,f71,f75,f77
  f77: plane 40.6x0.31mm, normal (0.72,0,-0.69), area 17.5mm2, adj f22,f24,f71,f76
  f78: plane 40.6x0.31mm, normal (-0.72,0,-0.69), area 17.5mm2, adj f22,f23,f71,f79
  f79: plane 40.6x0.19mm, normal (-1,0,0), area 7.7mm2, adj f22,f71,f75,f78
  f80: plane 3.29x2mm, normal (-0.73,0,-0.68), area 8.9mm2, adj f21,f22,f29,f82
  f81: plane 3.29x2mm, normal (0.73,0,-0.68), area 8.9mm2, adj f21,f22,f29,f82
  f82: plane 5x3.34mm, normal (0,0,-1), area 16.6mm2, adj f21,f22,f80,f81
  f83: plane 3.64x3.57mm, normal (-0.52,0.52,-0.68), area 8.9mm2, adj f18,f21,f28,f85
  f84: plane 3.64x3.57mm, normal (0.52,-0.52,-0.68), area 8.9mm2, adj f18,f21,f28,f85
  f85: plane 5.86x5.86mm, normal (0,0,-1), area 16.6mm2, adj f18,f21,f83,f84
  f86: plane 3.29x2mm, normal (0,0.73,-0.68), area 8.9mm2, adj f15,f21,f27,f88
  f87: plane 3.29x2mm, normal (0,-0.73,-0.68), area 8.9mm2, adj f15,f21,f27,f88
  f88: plane 5x3.34mm, normal (0,0,-1), area 16.6mm2, adj f15,f21,f86,f87
  f89: plane 3.64x3.57mm, normal (0.52,0.52,-0.68), area 8.9mm2, adj f12,f21,f26,f91
  f90: plane 3.64x3.57mm, normal (-0.52,-0.52,-0.68), area 8.9mm2, adj f12,f21,f26,f91
  f91: plane 5.86x5.86mm, normal (0,0,-1), area 16.6mm2, adj f12,f21,f89,f90
  f92: plane 3.29x2mm, normal (0.73,0,-0.68), area 8.9mm2, adj f9,f21,f25,f94
  f93: plane 3.29x2mm, normal (-0.73,0,-0.68), area 8.9mm2, adj f9,f21,f25,f94
  f94: plane 5x3.34mm, normal (0,0,-1), area 16.6mm2, adj f9,f21,f92,f93
  f95: plane 3.64x3.57mm, normal (0.52,-0.52,-0.68), area 8.9mm2, adj f6,f21,f32,f97
  f96: plane 3.64x3.57mm, normal (-0.52,0.52,-0.68), area 8.9mm2, adj f6,f21,f32,f97
  f97: plane 5.86x5.86mm, normal (0,0,-1), area 16.6mm2, adj f6,f21,f95,f96
  f98: plane 3.29x2mm, normal (0,-0.73,-0.68), area 8.9mm2, adj f3,f21,f31,f100
  f99: plane 3.29x2mm, normal (0,0.73,-0.68), area 8.9mm2, adj f3,f21,f31,f100
  f100: plane 5x3.34mm, normal (0,0,-1), area 16.6mm2, adj f3,f21,f98,f99
  f101: plane 3.64x3.57mm, normal (-0.52,-0.52,-0.68), area 8.9mm2, adj f0,f21,f30,f103
  f102: plane 3.64x3.57mm, normal (0.52,0.52,-0.68), area 8.9mm2, adj f0,f21,f30,f103
  f103: plane 5.86x5.86mm, normal (0,0,-1), area 16.6mm2, adj f0,f21,f101,f102
  f104: plane 28.71x28.71mm, normal (0.71,-0.71,0), area 7.7mm2, adj f18,f70,f75,f105
  f105: plane 28.92x28.92mm, normal (0.51,-0.51,-0.69), area 17.5mm2, adj f18,f20,f70,f104
  f106: plane 28.92x28.92mm, normal (-0.51,0.51,-0.69), area 17.5mm2, adj f18,f19,f70,f107
  f107: plane 28.71x28.71mm, normal (-0.71,0.71,0), area 7.7mm2, adj f18,f70,f75,f106
  f108: plane 40.6x0.19mm, normal (0,-1,0), area 7.7mm2, adj f15,f69,f75,f109
  f109: plane 40.6x0.31mm, normal (0,-0.72,-0.69), area 17.5mm2, adj f15,f17,f69,f108
  f110: plane 40.6x0.31mm, normal (0,0.72,-0.69), area 17.5mm2, adj f15,f16,f69,f111
  f111: plane 40.6x0.19mm, normal (0,1,0), area 7.7mm2, adj f15,f69,f75,f110
  f112: plane 28.71x28.71mm, normal (-0.71,-0.71,0), area 7.7mm2, adj f12,f68,f75,f113
  f113: plane 28.92x28.92mm, normal (-0.51,-0.51,-0.69), area 17.5mm2, adj f12,f14,f68,f112
  f114: plane 28.92x28.92mm, normal (0.51,0.51,-0.69), area 17.5mm2, adj f12,f13,f68,f115
  f115: plane 28.71x28.71mm, normal (0.71,0.71,0), area 7.7mm2, adj f12,f68,f75,f114
  f116: plane 40.6x0.19mm, normal (-1,0,0), area 7.7mm2, adj f9,f67,f75,f117
  f117: plane 40.6x0.31mm, normal (-0.72,0,-0.69), area 17.5mm2, adj f9,f11,f67,f116
  f118: plane 40.6x0.31mm, normal (0.72,0,-0.69), area 17.5mm2, adj f9,f10,f67,f119
  f119: plane 40.6x0.19mm, normal (1,0,0), area 7.7mm2, adj f9,f67,f75,f118
  f120: plane 28.71x28.71mm, normal (-0.71,0.71,0), area 7.7mm2, adj f6,f74,f75,f121
  f121: plane 28.92x28.92mm, normal (-0.51,0.51,-0.69), area 17.5mm2, adj f6,f8,f74,f120
  f122: plane 28.92x28.92mm, normal (0.51,-0.51,-0.69), area 17.5mm2, adj f6,f7,f74,f123
  f123: plane 28.71x28.71mm, normal (0.71,-0.71,0), area 7.7mm2, adj f6,f74,f75,f122
  f124: plane 40.6x0.19mm, normal (0,1,0), area 7.7mm2, adj f3,f73,f75,f125
  f125: plane 40.6x0.31mm, normal (0,0.72,-0.69), area 17.5mm2, adj f3,f5,f73,f124
  f126: plane 40.6x0.31mm, normal (0,-0.72,-0.69), area 17.5mm2, adj f3,f4,f73,f127
  f127: plane 40.6x0.19mm, normal (0,-1,0), area 7.7mm2, adj f3,f73,f75,f126
  f128: plane 28.71x28.71mm, normal (0.71,0.71,0), area 7.7mm2, adj f0,f72,f75,f129
  f129: plane 28.92x28.92mm, normal (0.51,0.51,-0.69), area 17.5mm2, adj f0,f2,f72,f128
  f130: plane 28.92x28.92mm, normal (-0.51,-0.51,-0.69), area 17.5mm2, adj f0,f1,f72,f131
  f131: plane 28.71x28.71mm, normal (-0.71,-0.71,0), area 7.7mm2, adj f0,f72,f75,f130
  f132: cone r=61.94mm half-angle=43deg, axis (0,0,1), area 1048.2mm2, adj f21,f66
  f133: cone r=4.1mm half-angle=45deg, axis (0,0,1), area 90.6mm2, adj f57,f75
PART C: 4 faces, bbox 22.2x22.2x7 mm
  f0: cylinder r=4.1mm len=8.2mm, axis (0,0,-1), area 180.3mm2, adj f2,f3
  f1: cylinder r=11.1mm len=22.2mm, axis (0,0,-1), area 488.2mm2, adj f2,f3
  f2: plane 22.2x22.2mm, normal (0,0,1), area 334.3mm2, adj f0,f1
  f3: plane 22.2x22.2mm, normal (0,0,-1), area 334.3mm2, adj f0,f1
PART D: 3 faces, bbox 8.2x8.2x80 mm
  f0: cylinder r=4.1mm len=80mm, axis (0,0,1), area 2060.9mm2, adj f1,f2
  f1: plane 8.2x8.2mm, normal (0,0,-1), area 52.8mm2, adj f0
  f2: plane 8.2x8.2mm, normal (0,0,1), area 52.8mm2, adj f0
PLACE A t=(3.15,-4.15,-12.2)mm fixed
PLACE B rot(axis=(-1,0.02,0),180deg) t=(3.15,-4.15,10.1)mm
PLACE C t=(3.15,-4.15,-4.5)mm
PLACE D rot(axis=(0,0,1),8.6deg) t=(3.15,-4.15,2.5)mm
MATE revolute B.f21 <-> D.f0  axis (0,0,-1) through (3.15,-4.15,2.5)mm
MATE cylindrical D.f0 <-> C.f1  axis (0,0,1) through (3.15,-4.15,2.5)mm
MATE fastened C.f0 <-> A.f1  axis (0,0,1) through (3.15,-4.15,2.5)mm
MATE revolute B.f21 <-> A.f1  axis (0,0,-1) through (3.15,-4.15,2.5)mm
